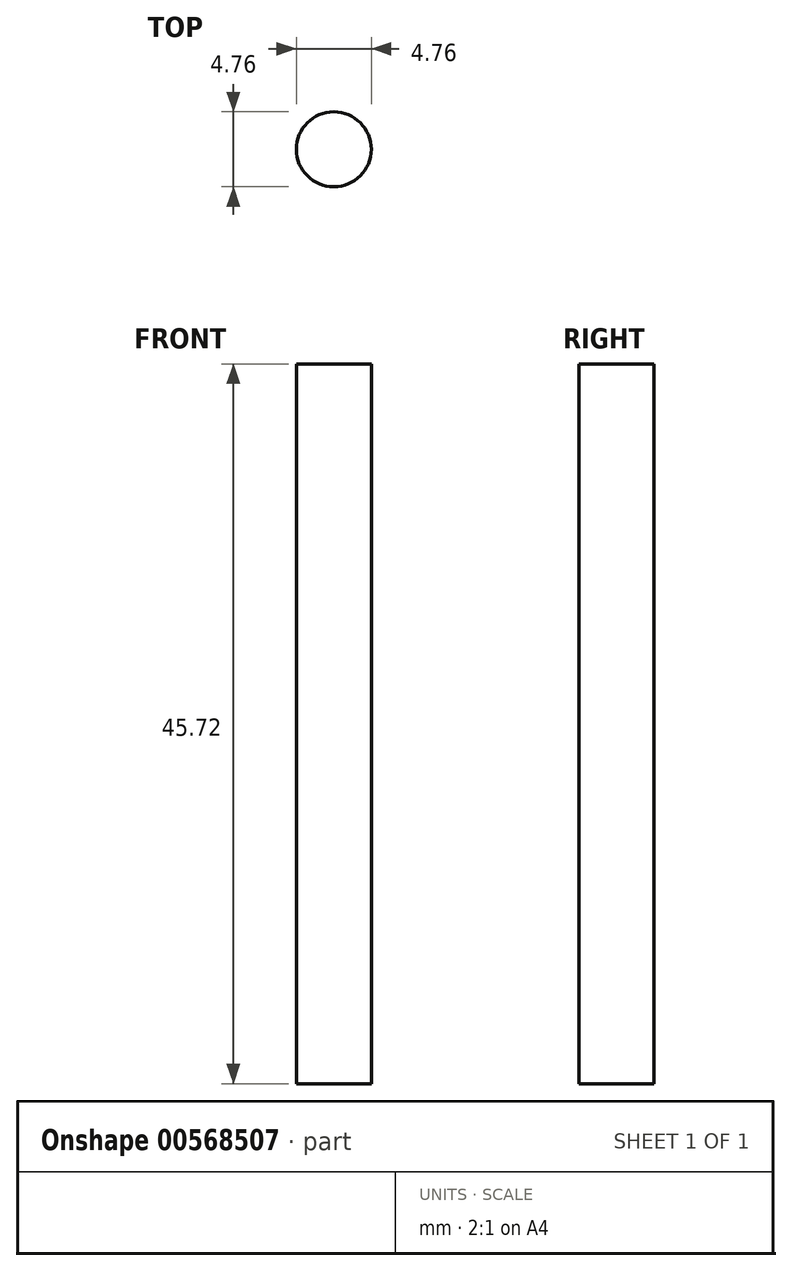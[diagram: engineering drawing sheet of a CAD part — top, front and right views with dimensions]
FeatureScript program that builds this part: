
annotation { "Feature Type Name" : "Feature", "Feature Type Description" : "" }
export const myFeature = defineFeature(function(context is Context, id is Id, definition is map)
    precondition{}
    {
        {
            var Q0;
            Q0=qCreatedBy(makeId("Top.planeOp"),FACE);
            var sketch = newSketch(context, id + "F0", { "sketchPlane" : qUnion([Q0])});
            skCircle(sketch, "E0", {"center": v(0, 0) * mm, "radius": 2.38 * mm});
            skSolve(sketch);
        }
        {
            var Q0;
            Q0 = qSketchRegion(id + "F0", true);
            extrude(context, id + "F1", {"entities" : qUnion([Q0]), "depth" : 45.72 * mm, "offsetDistance" : 25.4 * mm});
        }
    });
